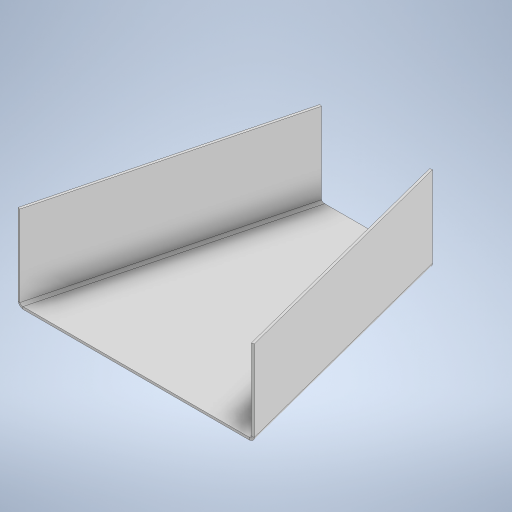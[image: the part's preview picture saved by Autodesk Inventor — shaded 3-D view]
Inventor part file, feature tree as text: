
AUTODESK INVENTOR PART (.ipt)
format: ipt  version: 2024.3 (Build 283343000, 343)  size: 291,328 bytes
history: native  units: mm
features: sheet_metal_op x7, other x4, sketch x3
ambient origin geometry x8: Origin, YZ Plane, XZ Plane, XY Plane, X Axis, Y Axis, Z Axis, Center Point
bodies: Solid1 (feature_tree)
feature tree (14):
  sheet_metal_op  "Face1"
  sheet_metal_op  "Flange1"
  sheet_metal_op  "Flange2"
  sketch  "Sketch1"  dims[d0=200.0mm]
  other  "Plate1"
  sketch  "Sketch2"  dims[d1=197.0mm]
  other  "Plate2"
  sheet_metal_op  "Bend1"
  sheet_metal_op  "Corner1"
  sketch  "Sketch3"  dims[d2=51.5mm d3=51.5mm d4=2.0mm d5=2.0mm d6=1.0mm d7=4.0mm d8=2.0mm d9=71.5mm d10=90.0deg d11=2.0mm d12=8.0mm d13=2.0mm d14=2.0mm d15=2.0mm d16=1.0mm d17=4.0mm d18=2.0mm d19=71.5mm d20=90.0deg d21=2.0mm d22=8.0mm d23=2.0mm d24=2.0mm]
  other  "Plate3"
  sheet_metal_op  "Bend2"
  sheet_metal_op  "Corner2"
  other  "Definition1"
